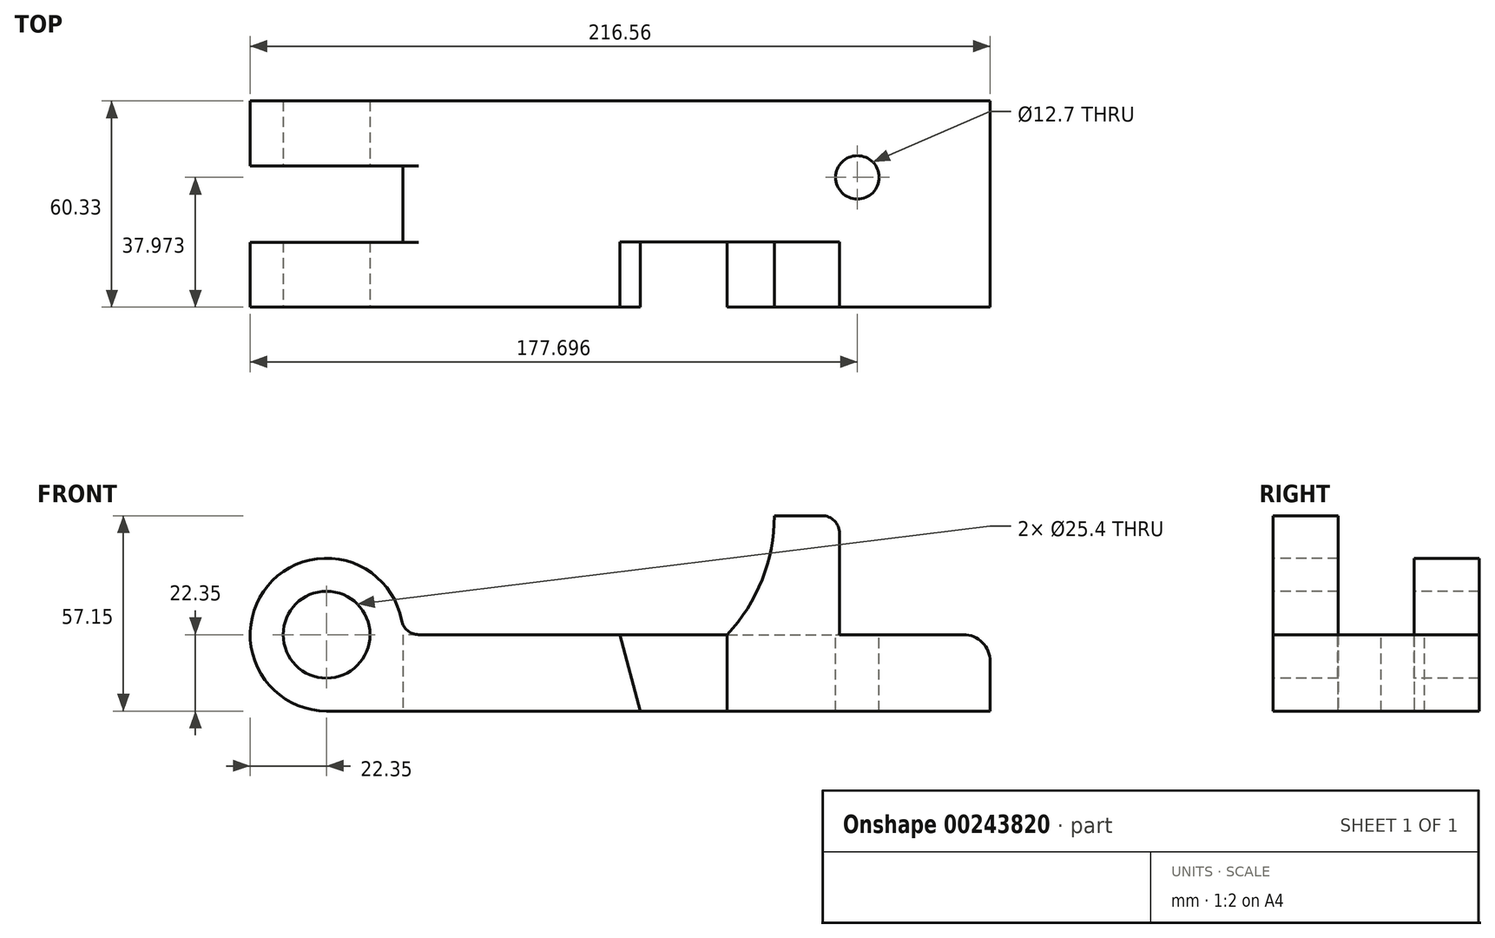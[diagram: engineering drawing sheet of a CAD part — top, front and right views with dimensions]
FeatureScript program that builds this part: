
annotation { "Feature Type Name" : "Feature", "Feature Type Description" : "" }
export const myFeature = defineFeature(function(context is Context, id is Id, definition is map)
    precondition{}
    {
        {
            var Q0;
            Q0=qCreatedBy(makeId("Front.planeOp"),FACE);
            var sketch = newSketch(context, id + "F0", { "sketchPlane" : qUnion([Q0])});
            skCircle(sketch, "E0", {"center": v(0, 0) * mm, "radius": 12.7 * mm});
            skArc(sketch, "E1", {"start": v(22.35, 0) * mm, "mid": v(-15.8, 15.8) * mm, "end": v(0, -22.35) * mm});
            skLineSegment(sketch, "E2", {"start": v(0, -22.35) * mm, "end": v(194.2, -22.35) * mm});
            skLineSegment(sketch, "E3", {"start": v(194.2, -22.35) * mm, "end": v(194.2, 0) * mm});
            skLineSegment(sketch, "E4", {"start": v(22.35, 0) * mm, "end": v(117.25, 0) * mm});
            skLineSegment(sketch, "E5", {"start": v(194.2, 0) * mm, "end": v(150.09, 0) * mm});
            skLineSegment(sketch, "E6", {"start": v(150.09, 0) * mm, "end": v(150.09, 34.8) * mm});
            skLineSegment(sketch, "E7", {"start": v(150.09, 34.8) * mm, "end": v(131.04, 34.8) * mm});
            skArc(sketch, "E8", {"start": v(117.25, 0) * mm, "mid": v(127.46, 16.08) * mm, "end": v(131.04, 34.8) * mm});
            skLineSegment(sketch, "E9", {"start": v(117.25, 0) * mm, "end": v(117.25, -22.35) * mm});
            skLineSegment(sketch, "E10", {"start": v(85.85, 0) * mm, "end": v(91.85, -22.35) * mm});
            skSolve(sketch);
        }
        {
            var Q0;
            Q0=makeQuery(id+"F0.imprint","IMPRINT",FACE,{"disambiguationData":[TD([[makeQuery(id+"F0.imprint","IMPRINT",EDGE,{"derivedFrom":sQuery(id+"F0.wireOp",EDGE,"E0")}),-1.0]])]});
            var Q1;
            {var subQ0=sQuery(id+"F0.wireOp",EDGE,"E9");Q1=makeQuery(id+"F0.imprint","IMPRINT",FACE,{"disambiguationData":[TD([[makeQuery(id+"F0.imprint","IMPRINT",EDGE,{"derivedFrom":subQ0}),-1.0]])]});}
            var Q2;
            {var subQ0=sQuery(id+"F0.wireOp",EDGE,"E3");Q2=makeQuery(id+"F0.imprint","IMPRINT",FACE,{"disambiguationData":[TD([[makeQuery(id+"F0.imprint","IMPRINT",EDGE,{"derivedFrom":subQ0}),1.0]])]});}
            extrude(context, id + "F1", {"entities" : qUnion([Q0, Q1, Q2]), "oppositeDirection" : true, "depth" : 60.32 * mm});
        }
        {
            var Q0;
            {var subQ0=sQuery(id+"F0.wireOp",EDGE,"E9");Q0=makeQuery(id+"F0.imprint","IMPRINT",FACE,{"disambiguationData":[TD([[makeQuery(id+"F0.imprint","IMPRINT",EDGE,{"derivedFrom":subQ0}),-1.0]])]});}
            extrude(context, id + "F2", {"entities" : qUnion([Q0]), "operationType" : NewBodyOperationType.REMOVE, "oppositeDirection" : true, "depth" : 19.05 * mm});
        }
        {
            var Q0;
            Q0=makeQuery(id+"F1.opExtrude","SWEPT_FACE",FACE,{"disambiguationData":[OSD([sQuery(id+"F0.wireOp",EDGE,"E6")])]});
            var sketch = newSketch(context, id + "F3", { "sketchPlane" : qUnion([Q0])});
            skLineSegment(sketch, "E11", {"start": v(60.33, 34.8) * mm, "end": v(19.05, 34.8) * mm});
            skLineSegment(sketch, "E12", {"start": v(19.05, 34.8) * mm, "end": v(19.05, 0) * mm});
            skLineSegment(sketch, "E13", {"start": v(19.05, 0) * mm, "end": v(60.33, 0) * mm});
            skLineSegment(sketch, "E14", {"start": v(60.33, 0) * mm, "end": v(60.33, 34.8) * mm});
            skSolve(sketch);
        }
        {
            var Q0;
            Q0=makeQuery(id+"F3.imprint","IMPRINT",FACE,{"disambiguationData":[TD([[makeQuery(id+"F3.imprint","IMPRINT",EDGE,{"derivedFrom":sQuery(id+"F3.wireOp",EDGE,"E11")}),1.0]])]});
            extrude(context, id + "F4", {"entities" : qUnion([Q0]), "operationType" : NewBodyOperationType.REMOVE, "oppositeDirection" : true, "depth" : 50.8 * mm});
        }
        {
            var Q0;
            Q0=qCreatedBy(makeId("Top.planeOp"),FACE);
            var sketch = newSketch(context, id + "F5", { "sketchPlane" : qUnion([Q0])});
            skLineSegment(sketch, "E15", {"start": v(22.35, 41.33) * mm, "end": v(-32.94, 41.33) * mm});
            skLineSegment(sketch, "E16", {"start": v(22.35, 19) * mm, "end": v(-32.94, 19) * mm});
            skLineSegment(sketch, "E17", {"start": v(-32.94, 19) * mm, "end": v(-32.94, 41.33) * mm});
            skLineSegment(sketch, "E18", {"start": v(22.35, 41.33) * mm, "end": v(22.35, 19) * mm});
            skSolve(sketch);
        }
        {
            var Q0;
            Q0=makeQuery(id+"F5.imprint","IMPRINT",FACE,{"disambiguationData":[TD([[makeQuery(id+"F5.imprint","IMPRINT",EDGE,{"derivedFrom":sQuery(id+"F5.wireOp",EDGE,"E15")}),1.0]])]});
            extrude(context, id + "F6", {"entities" : qUnion([Q0]), "operationType" : NewBodyOperationType.REMOVE, "endBound" : BoundingType.SYMMETRIC, "depth" : 127 * mm});
        }
        {
            var Q0;
            Q0=makeQuery(id+"F4.boolean.opBoolean","MERGE",FACE,{"derivedFrom":[makeQuery(id+"F1.opExtrude","SWEPT_FACE",FACE,{"disambiguationData":[OSD([sQuery(id+"F0.wireOp",EDGE,"E5")])]}),makeQuery(id+"F1.opExtrude","SWEPT_FACE",FACE,{"disambiguationData":[OSD([sQuery(id+"F0.wireOp",EDGE,"E4")])]}),makeQuery(id+"F4.opExtrude","SWEPT_FACE",FACE,{"disambiguationData":[OSD([sQuery(id+"F3.wireOp",EDGE,"E13")])]})]});
            var sketch = newSketch(context, id + "F7", { "sketchPlane" : qUnion([Q0])});
            skCircle(sketch, "E19", {"center": v(155.35, 37.97) * mm, "radius": 6.35 * mm});
            skSolve(sketch);
        }
        {
            var Q0;
            Q0=makeQuery(id+"F7.imprint","IMPRINT",FACE,{"disambiguationData":[TD([[makeQuery(id+"F7.imprint","IMPRINT",EDGE,{"derivedFrom":sQuery(id+"F7.wireOp",EDGE,"E19")}),1.0]])]});
            extrude(context, id + "F8", {"entities" : qUnion([Q0]), "operationType" : NewBodyOperationType.REMOVE, "oppositeDirection" : true, "depth" : 127 * mm});
        }
        {
            var Q0;
            Q0=makeQuery(id+"F1.opExtrude","SWEPT_EDGE",EDGE,{"disambiguationData":[OSD([sQuery(id+"F0.wireOp",EDGE,"E3"),sQuery(id+"F0.wireOp",EDGE,"E5")])]});
            fillet(context, id + "F9", {"entities" : qUnion([Q0]), "radius" : 7.87 * mm, "tangentPropagation" : true, "allowEdgeOverflow" : false});
        }
        {
            var Q0;
            Q0=makeQuery(id+"F1.opExtrude","SWEPT_EDGE",EDGE,{"disambiguationData":[OSD([sQuery(id+"F0.wireOp",EDGE,"E6"),sQuery(id+"F0.wireOp",EDGE,"E7")])]});
            fillet(context, id + "F10", {"entities" : qUnion([Q0]), "radius" : 5.08 * mm, "tangentPropagation" : true, "allowEdgeOverflow" : false});
        }
        {
            var Q0;
            {var subQ0=sQuery(id+"F0.wireOp",EDGE,"E5");var subQ1=sQuery(id+"F0.wireOp",EDGE,"E4");var subQ2=sQuery(id+"F0.wireOp",EDGE,"E1");Q0=makeQuery(id+"F6.boolean.opBoolean","SPLIT",EDGE,{"disambiguationData":[TD([makeQuery(id+"F1.opExtrude","CAP_FACE",FACE,{"disambiguationData":[OSD([sQuery(id+"F0.wireOp",EDGE,"E0"),subQ2,sQuery(id+"F0.wireOp",EDGE,"E2"),sQuery(id+"F0.wireOp",EDGE,"E3"),subQ1,subQ0,sQuery(id+"F0.wireOp",EDGE,"E6"),sQuery(id+"F0.wireOp",EDGE,"E7"),sQuery(id+"F0.wireOp",EDGE,"E8")])],"isStart":true}),makeQuery(id+"F1.opExtrude","SWEPT_FACE",FACE,{"disambiguationData":[OSD([subQ2])]}),makeQuery(id+"F1.opExtrude","SWEPT_FACE",FACE,{"disambiguationData":[OSD([subQ1])]}),makeQuery(id+"F1.opExtrude","SWEPT_FACE",FACE,{"disambiguationData":[OSD([subQ0])]}),makeQuery(id+"F4.opExtrude","SWEPT_FACE",FACE,{"disambiguationData":[OSD([sQuery(id+"F3.wireOp",EDGE,"E13")])]}),makeQuery(id+"F6.opExtrude","SWEPT_FACE",FACE,{"disambiguationData":[OSD([sQuery(id+"F5.wireOp",EDGE,"E16")])]}),makeQuery(id+"F6.opExtrude","SWEPT_FACE",FACE,{"disambiguationData":[OSD([sQuery(id+"F5.wireOp",EDGE,"E18")])]})])],"derivedFrom":makeQuery(id+"F1.opExtrude","SWEPT_EDGE",EDGE,{"disambiguationData":[OSD([subQ2,subQ1])]})});}
            var Q1;
            {var subQ0=sQuery(id+"F0.wireOp",EDGE,"E5");var subQ1=sQuery(id+"F0.wireOp",EDGE,"E4");var subQ2=sQuery(id+"F0.wireOp",EDGE,"E1");Q1=makeQuery(id+"F6.boolean.opBoolean","SPLIT",EDGE,{"disambiguationData":[TD([makeQuery(id+"F1.opExtrude","CAP_FACE",FACE,{"disambiguationData":[OSD([sQuery(id+"F0.wireOp",EDGE,"E0"),subQ2,sQuery(id+"F0.wireOp",EDGE,"E2"),sQuery(id+"F0.wireOp",EDGE,"E3"),subQ1,subQ0,sQuery(id+"F0.wireOp",EDGE,"E6"),sQuery(id+"F0.wireOp",EDGE,"E7"),sQuery(id+"F0.wireOp",EDGE,"E8")])],"isStart":false}),makeQuery(id+"F1.opExtrude","SWEPT_FACE",FACE,{"disambiguationData":[OSD([subQ2])]}),makeQuery(id+"F1.opExtrude","SWEPT_FACE",FACE,{"disambiguationData":[OSD([subQ1])]}),makeQuery(id+"F1.opExtrude","SWEPT_FACE",FACE,{"disambiguationData":[OSD([subQ0])]}),makeQuery(id+"F4.opExtrude","SWEPT_FACE",FACE,{"disambiguationData":[OSD([sQuery(id+"F3.wireOp",EDGE,"E13")])]}),makeQuery(id+"F6.opExtrude","SWEPT_FACE",FACE,{"disambiguationData":[OSD([sQuery(id+"F5.wireOp",EDGE,"E15")])]}),makeQuery(id+"F6.opExtrude","SWEPT_FACE",FACE,{"disambiguationData":[OSD([sQuery(id+"F5.wireOp",EDGE,"E18")])]})])],"derivedFrom":makeQuery(id+"F1.opExtrude","SWEPT_EDGE",EDGE,{"disambiguationData":[OSD([subQ2,subQ1])]})});}
            fillet(context, id + "F11", {"entities" : qUnion([Q0, Q1]), "radius" : 5.08 * mm, "tangentPropagation" : true, "allowEdgeOverflow" : false});
        }
    });
